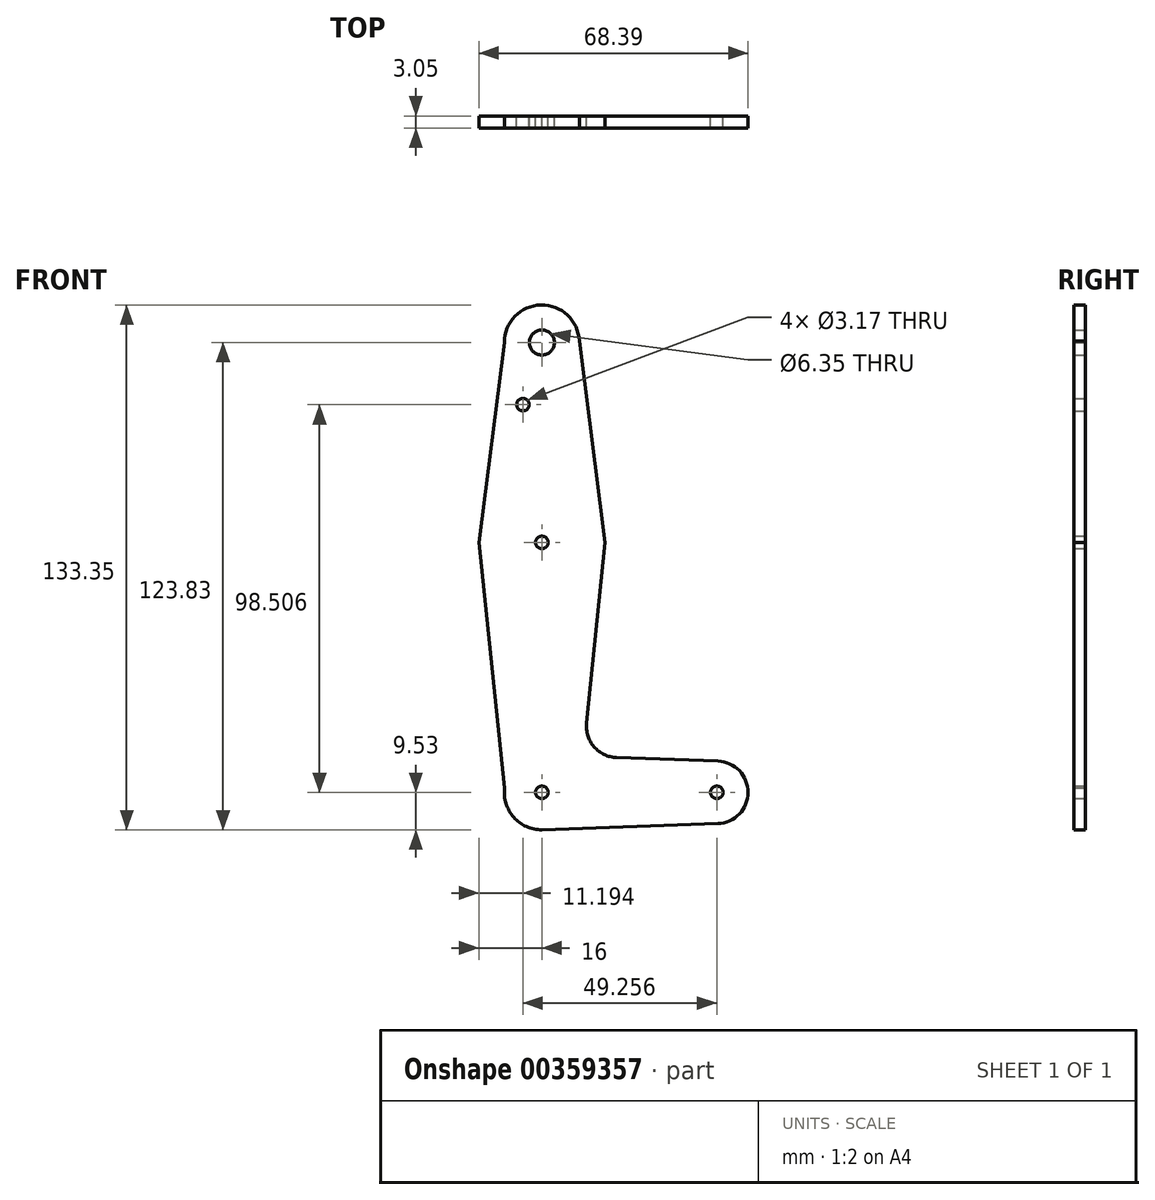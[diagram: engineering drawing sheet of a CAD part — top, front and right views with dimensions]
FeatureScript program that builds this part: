
annotation { "Feature Type Name" : "Feature", "Feature Type Description" : "" }
export const myFeature = defineFeature(function(context is Context, id is Id, definition is map)
    precondition{}
    {
        {
            var Q0;
            Q0=qCreatedBy(makeId("Front.planeOp"),FACE);
            var sketch = newSketch(context, id + "F0", { "sketchPlane" : qUnion([Q0])});
            skCircle(sketch, "E0", {"center": v(0, 50.8) * mm, "radius": 9.53 * mm});
            skCircle(sketch, "E1", {"center": v(0, 0) * mm, "radius": 15.88 * mm});
            skCircle(sketch, "E2", {"center": v(0, -63.5) * mm, "radius": 9.53 * mm});
            skLineSegment(sketch, "E3", {"start": v(-9.52, 50.79) * mm, "end": v(-16, 0) * mm});
            skLineSegment(sketch, "E4", {"start": v(9.52, 51.21) * mm, "end": v(16, 0) * mm});
            skLineSegment(sketch, "E5", {"start": v(-16, 0) * mm, "end": v(-9.46, -62.4) * mm});
            skLineSegment(sketch, "E6", {"start": v(16, 0) * mm, "end": v(11.35, -45.9) * mm});
            skCircle(sketch, "E7", {"center": v(44.45, -63.5) * mm, "radius": 7.94 * mm});
            skLineSegment(sketch, "E8", {"start": v(0, -73.03) * mm, "end": v(44.73, -71.43) * mm});
            skLineSegment(sketch, "E9", {"start": v(18.98, -54.65) * mm, "end": v(44.73, -55.57) * mm});
            skCircle(sketch, "E10", {"center": v(-4.8, 35) * mm, "radius": 1.59 * mm});
            skCircle(sketch, "E11", {"center": v(0, 0) * mm, "radius": 1.59 * mm});
            skCircle(sketch, "E12", {"center": v(0, -63.5) * mm, "radius": 1.59 * mm});
            skCircle(sketch, "E13", {"center": v(44.45, -63.5) * mm, "radius": 1.59 * mm});
            skPoint(sketch, "E14.newPointA", {"position": v(0, -53.98) * mm});
            skArc(sketch, "E14.filletArc", {"start": v(11.35, -45.9) * mm, "mid": v(13.27, -51.93) * mm, "end": v(18.98, -54.65) * mm});
            skCircle(sketch, "E15", {"center": v(0, 50.8) * mm, "radius": 3.18 * mm});
            skSolve(sketch);
        }
        {
            var Q0;
            Q0=makeQuery(id+"F0.imprint","IMPRINT",FACE,{"disambiguationData":[TD([[makeQuery(id+"F0.imprint","IMPRINT",EDGE,{"derivedFrom":sQuery(id+"F0.wireOp",EDGE,"E10")}),-1.0]])]});
            var Q1;
            Q1=makeQuery(id+"F0.imprint","IMPRINT",FACE,{"disambiguationData":[TD([[makeQuery(id+"F0.imprint","IMPRINT",EDGE,{"derivedFrom":sQuery(id+"F0.wireOp",EDGE,"E15")}),-1.0]])]});
            var Q2;
            Q2=makeQuery(id+"F0.imprint","IMPRINT",FACE,{"disambiguationData":[TD([[makeQuery(id+"F0.imprint","IMPRINT",EDGE,{"derivedFrom":sQuery(id+"F0.wireOp",EDGE,"E11")}),-1.0]])]});
            var Q3;
            {var subQ4=sQuery(id+"F0.wireOp",EDGE,"E5");Q3=makeQuery(id+"F0.imprint","IMPRINT",FACE,{"disambiguationData":[TD([[makeQuery(id+"F0.imprint","IMPRINT",EDGE,{"derivedFrom":subQ4}),1.0]])]});}
            var Q4;
            Q4=makeQuery(id+"F0.imprint","IMPRINT",FACE,{"disambiguationData":[TD([[makeQuery(id+"F0.imprint","IMPRINT",EDGE,{"derivedFrom":sQuery(id+"F0.wireOp",EDGE,"E12")}),-1.0]])]});
            var Q5;
            Q5=makeQuery(id+"F0.imprint","IMPRINT",FACE,{"disambiguationData":[TD([[makeQuery(id+"F0.imprint","IMPRINT",EDGE,{"derivedFrom":sQuery(id+"F0.wireOp",EDGE,"E13")}),-1.0]])]});
            extrude(context, id + "F1", {"entities" : qUnion([Q0, Q1, Q2, Q3, Q4, Q5]), "depth" : 3.05 * mm});
        }
    });
